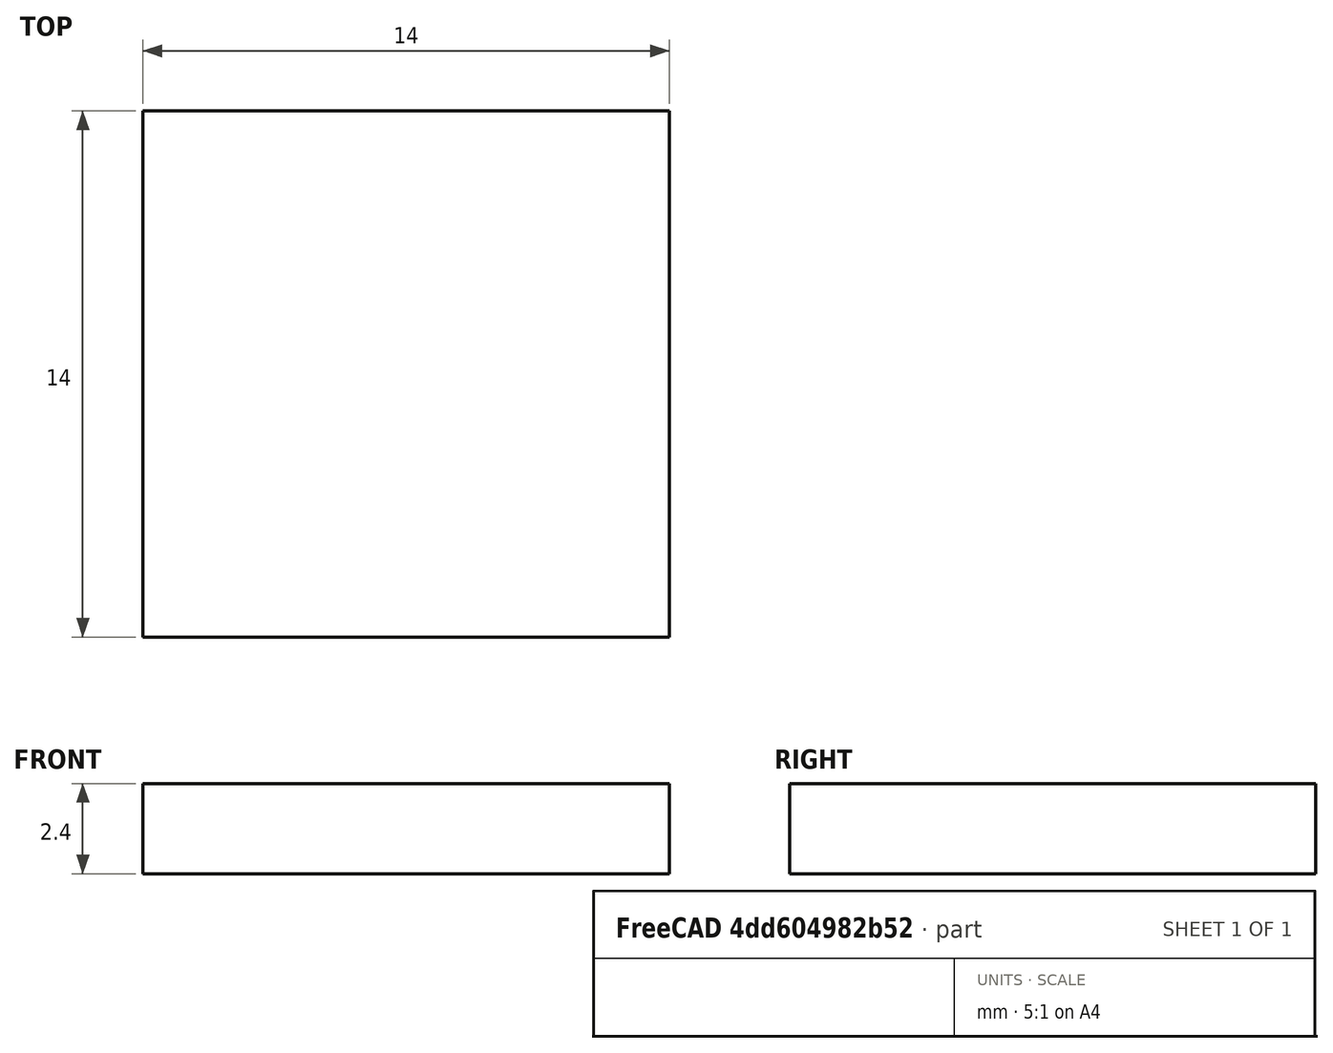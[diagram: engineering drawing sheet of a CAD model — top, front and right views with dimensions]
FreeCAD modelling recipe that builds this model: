
FCSTD DOCUMENT  (FreeCAD 0.18R16110 (Git))
Label: square2.4
License: All rights reserved
LicenseURL: http://en.wikipedia.org/wiki/All_rights_reserved
objects: Sketcher::SketchObject×1, Part::Extrusion×1
note: 2 computed .brp shape members not serialized (recipe doc carries the construction recipe); baked Part::Feature solids carry a one-line shape summary decoded from their .brp

FEATURE [Sketcher::SketchObject] Sketch
  sketch-geometry (4):
    g0: LineSegment StartX=-7 StartY=7 StartZ=0 EndX=7 EndY=7 EndZ=0
    g1: LineSegment StartX=7 StartY=7 StartZ=0 EndX=7 EndY=-7 EndZ=0
    g2: LineSegment StartX=7 StartY=-7 StartZ=0 EndX=-7 EndY=-7 EndZ=0
    g3: LineSegment StartX=-7 StartY=-7 StartZ=0 EndX=-7 EndY=7 EndZ=0
  constraints (10):
    c: Coincident(g0,g1)
    c: Coincident(g1,g2)
    c: Coincident(g2,g3)
    c: Coincident(g3,g0)
    c: Horizontal(g2)
    c: Vertical(g1)
    c: Symmetric(g0,g0,g-2)
    c: Symmetric(g2,g0,g-1)
    c: Distance(g0) = 14
    c: Distance(g3) = 14
FEATURE [Part::Extrusion] Extrude
  Base = -> Sketch
  Dir = (0,0,1)
  DirMode = 2
  FaceMakerClass = Part::FaceMakerBullseye
  LengthFwd = 2.4
  LengthRev = 0
  Solid = true
  Symmetric = false
